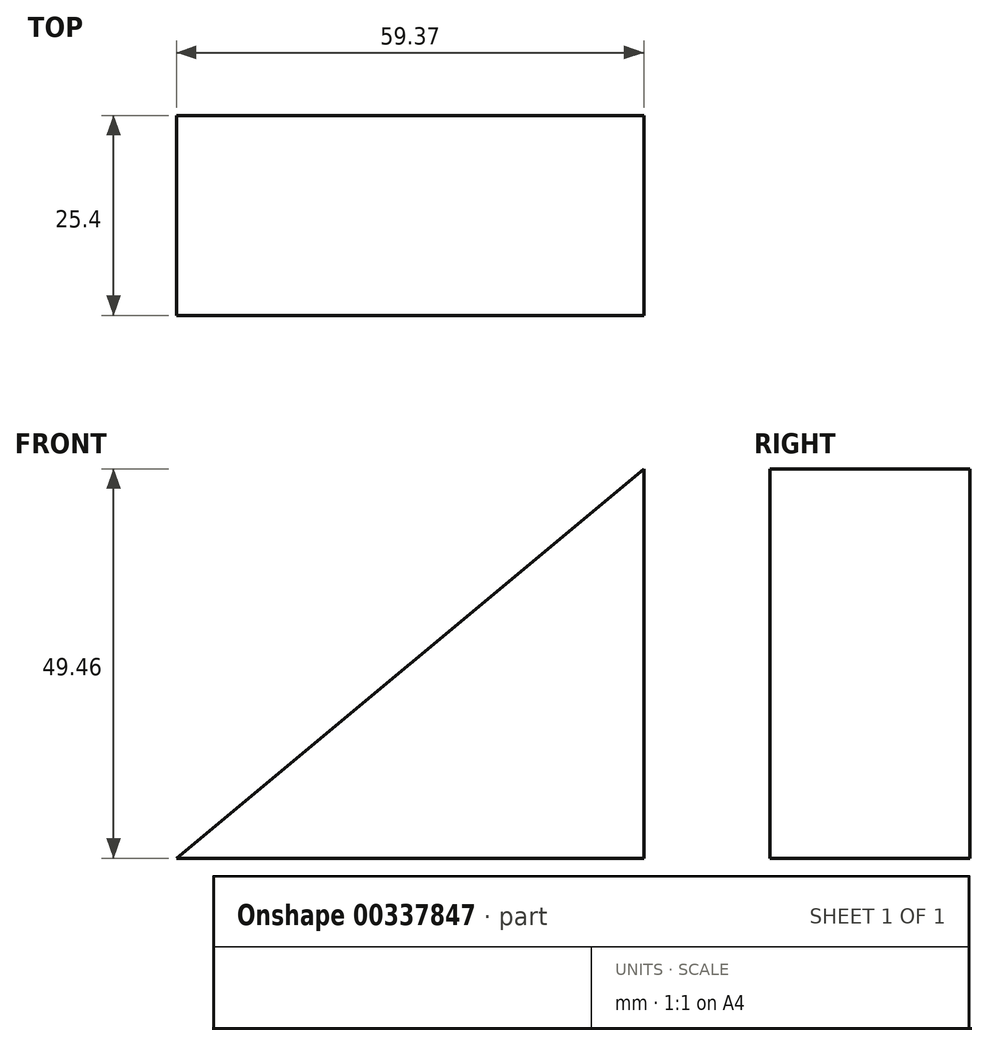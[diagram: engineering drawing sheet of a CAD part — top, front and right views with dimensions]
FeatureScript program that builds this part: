
annotation { "Feature Type Name" : "Feature", "Feature Type Description" : "" }
export const myFeature = defineFeature(function(context is Context, id is Id, definition is map)
    precondition{}
    {
        {
            var Q0;
            Q0=qCreatedBy(makeId("Front.planeOp"),FACE);
            var sketch = newSketch(context, id + "F0", { "sketchPlane" : qUnion([Q0])});
            skLineSegment(sketch, "E0", {"start": v(0, 0) * mm, "end": v(59.37, 49.46) * mm});
            skLineSegment(sketch, "E1", {"start": v(59.37, 49.46) * mm, "end": v(59.37, 0) * mm});
            skLineSegment(sketch, "E2", {"start": v(59.37, 0) * mm, "end": v(0, 0) * mm});
            skSolve(sketch);
        }
        {
            var Q0;
            Q0=makeQuery(id+"F0.imprint","IMPRINT",FACE,{"disambiguationData":[TD([[makeQuery(id+"F0.imprint","IMPRINT",EDGE,{"derivedFrom":sQuery(id+"F0.wireOp",EDGE,"E0")}),-1.0]])]});
            extrude(context, id + "F1", {"entities" : qUnion([Q0]), "endBound" : BoundingType.SYMMETRIC, "depth" : 25.4 * mm});
        }
    });
